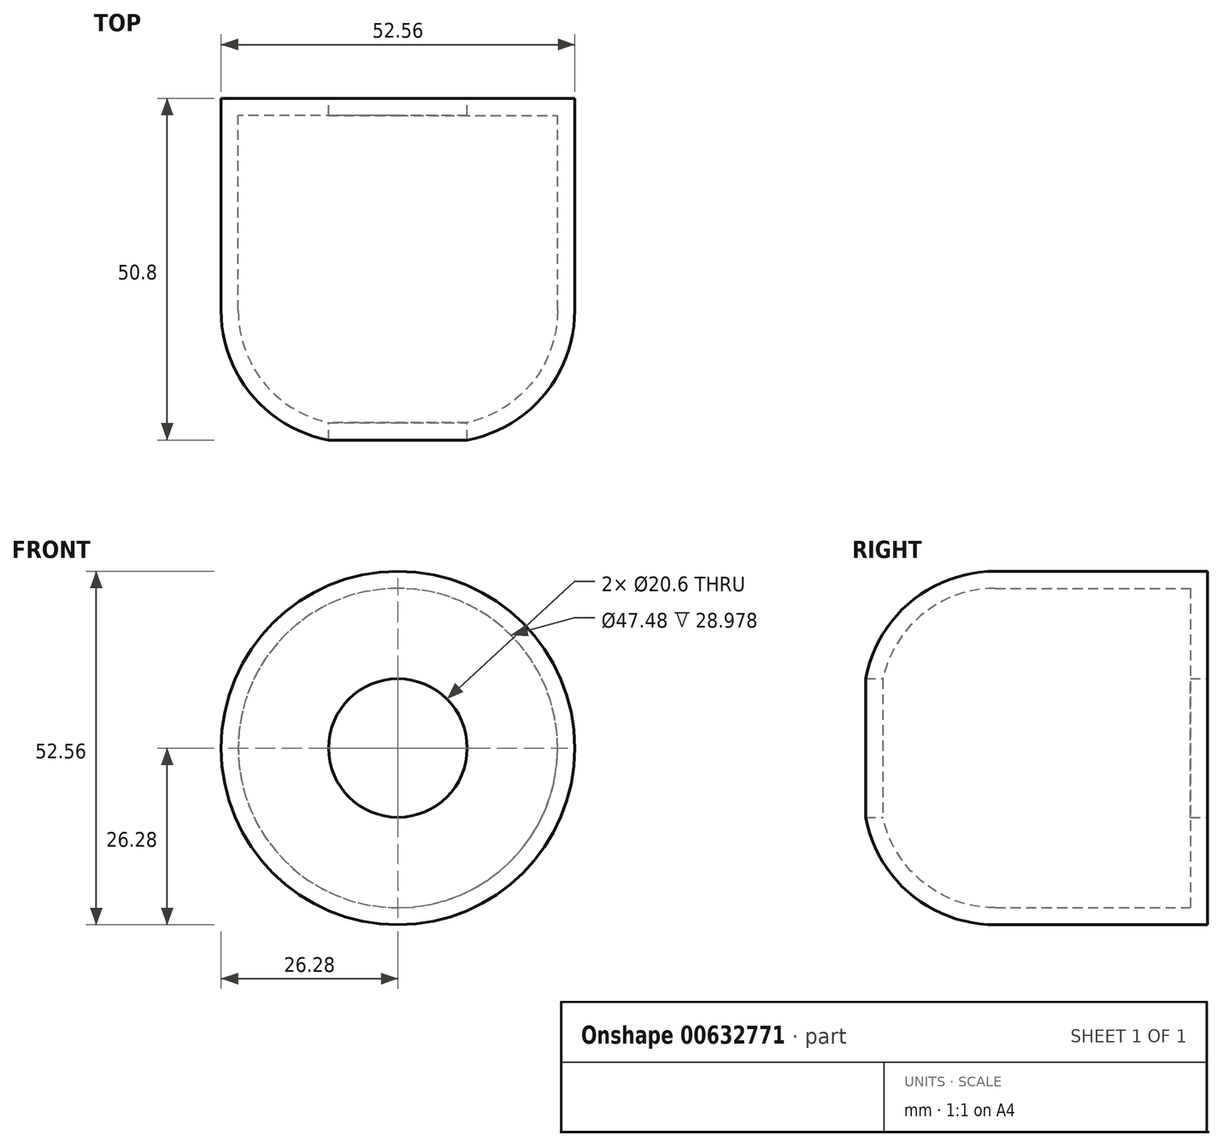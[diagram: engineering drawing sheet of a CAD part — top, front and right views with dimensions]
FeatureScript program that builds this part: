
annotation { "Feature Type Name" : "Feature", "Feature Type Description" : "" }
export const myFeature = defineFeature(function(context is Context, id is Id, definition is map)
    precondition{}
    {
        {
            var Q0;
            Q0=qCreatedBy(makeId("Front.planeOp"),FACE);
            var sketch = newSketch(context, id + "F0", { "sketchPlane" : qUnion([Q0])});
            skCircle(sketch, "E0", {"center": v(0, 0) * mm, "radius": 26.28 * mm});
            skCircle(sketch, "E1", {"center": v(0, 0) * mm, "radius": 10.3 * mm});
            skSolve(sketch);
        }
        {
            var Q0;
            Q0 = qSketchRegion(id + "F0", true);
            extrude(context, id + "F1", {"entities" : qUnion([Q0]), "depth" : 50.8 * mm, "offsetDistance" : 25.4 * mm});
        }
        {
            var Q0;
            Q0=makeQuery(id+"F1.opExtrude","CAP_EDGE",EDGE,{"disambiguationData":[OSD([sQuery(id+"F0.wireOp",EDGE,"E0")])],"isStart":false});
            fillet(context, id + "F2", {"entities" : qUnion([Q0]), "radius" : 19.62 * mm, "tangentPropagation" : true, "allowEdgeOverflow" : false});
        }
        {
            var Q0;
            Q0=makeQuery(id+"F1.opExtrude","SWEPT_FACE",FACE,{"disambiguationData":[OSD([sQuery(id+"F0.wireOp",EDGE,"E1")])]});
            shell(context, id + "F3", {"entities" : qUnion([Q0]), "thickness" : 2.54 * mm});
        }
    });
